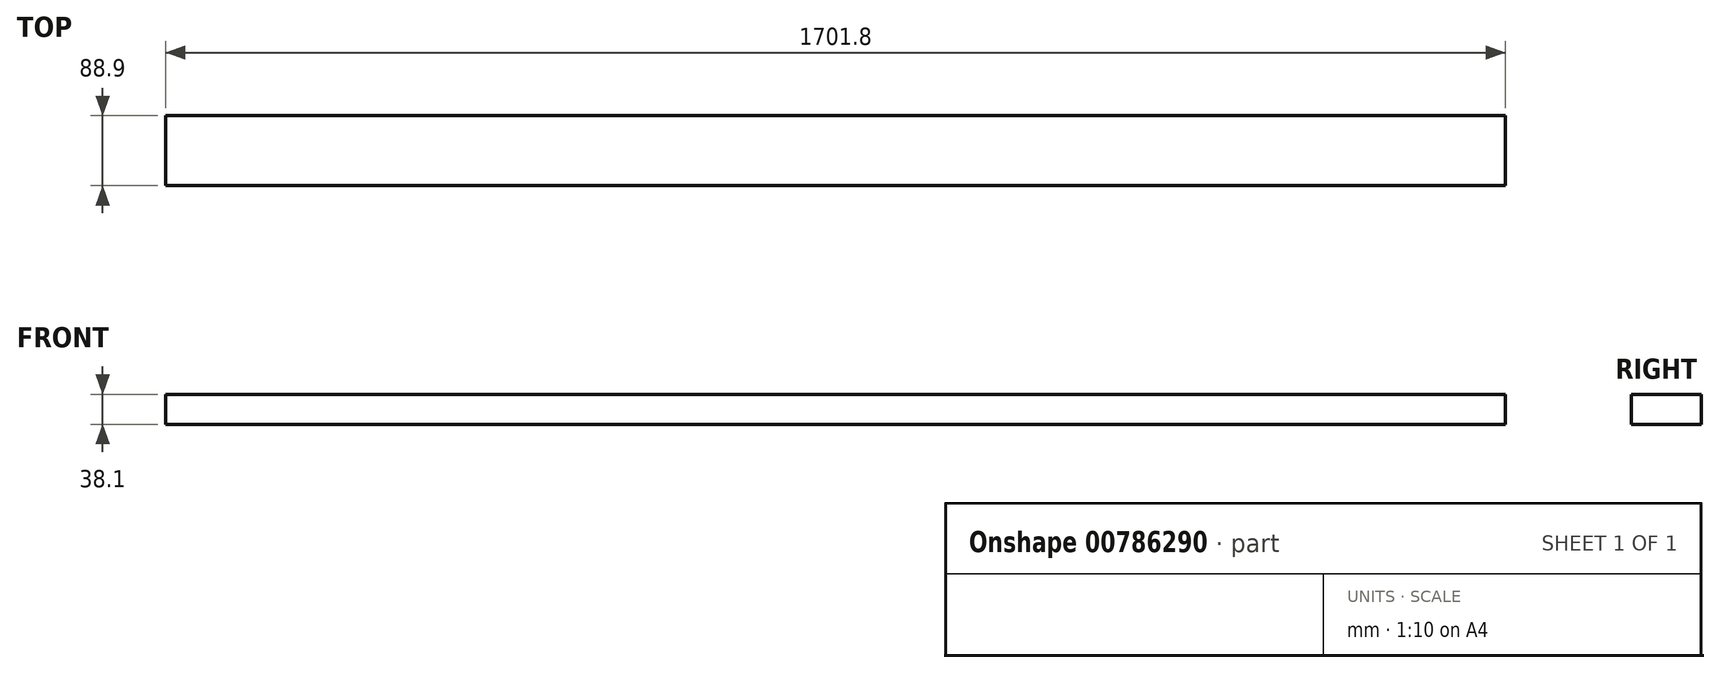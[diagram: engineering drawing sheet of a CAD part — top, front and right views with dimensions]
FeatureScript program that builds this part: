
annotation { "Feature Type Name" : "Feature", "Feature Type Description" : "" }
export const myFeature = defineFeature(function(context is Context, id is Id, definition is map)
    precondition{}
    {
        {
            var Q0;
            Q0=qCreatedBy(makeId("Front.planeOp"),FACE);
            var sketch = newSketch(context, id + "F0", { "sketchPlane" : qUnion([Q0])});
            skLineSegment(sketch, "E0.bottom", {"start": v(-850.9, 19.05) * mm, "end": v(850.9, 19.05) * mm});
            skLineSegment(sketch, "E0.top", {"start": v(-850.9, -19.05) * mm, "end": v(850.9, -19.05) * mm});
            skLineSegment(sketch, "E0.left", {"start": v(-850.9, 19.05) * mm, "end": v(-850.9, -19.05) * mm});
            skLineSegment(sketch, "E0.right", {"start": v(850.9, 19.05) * mm, "end": v(850.9, -19.05) * mm});
            skPoint(sketch, "E0.middle", {"position": v(0, 0) * mm});
            skSolve(sketch);
        }
        {
            var Q0;
            Q0=makeQuery(id+"F0.imprint","IMPRINT",FACE,{"disambiguationData":[TD([[makeQuery(id+"F0.imprint","IMPRINT",EDGE,{"derivedFrom":sQuery(id+"F0.wireOp",EDGE,"E0.bottom")}),-1.0]])]});
            extrude(context, id + "F1", {"entities" : qUnion([Q0]), "endBound" : BoundingType.SYMMETRIC, "depth" : 88.9 * mm, "offsetDistance" : 25.4 * mm});
        }
    });
